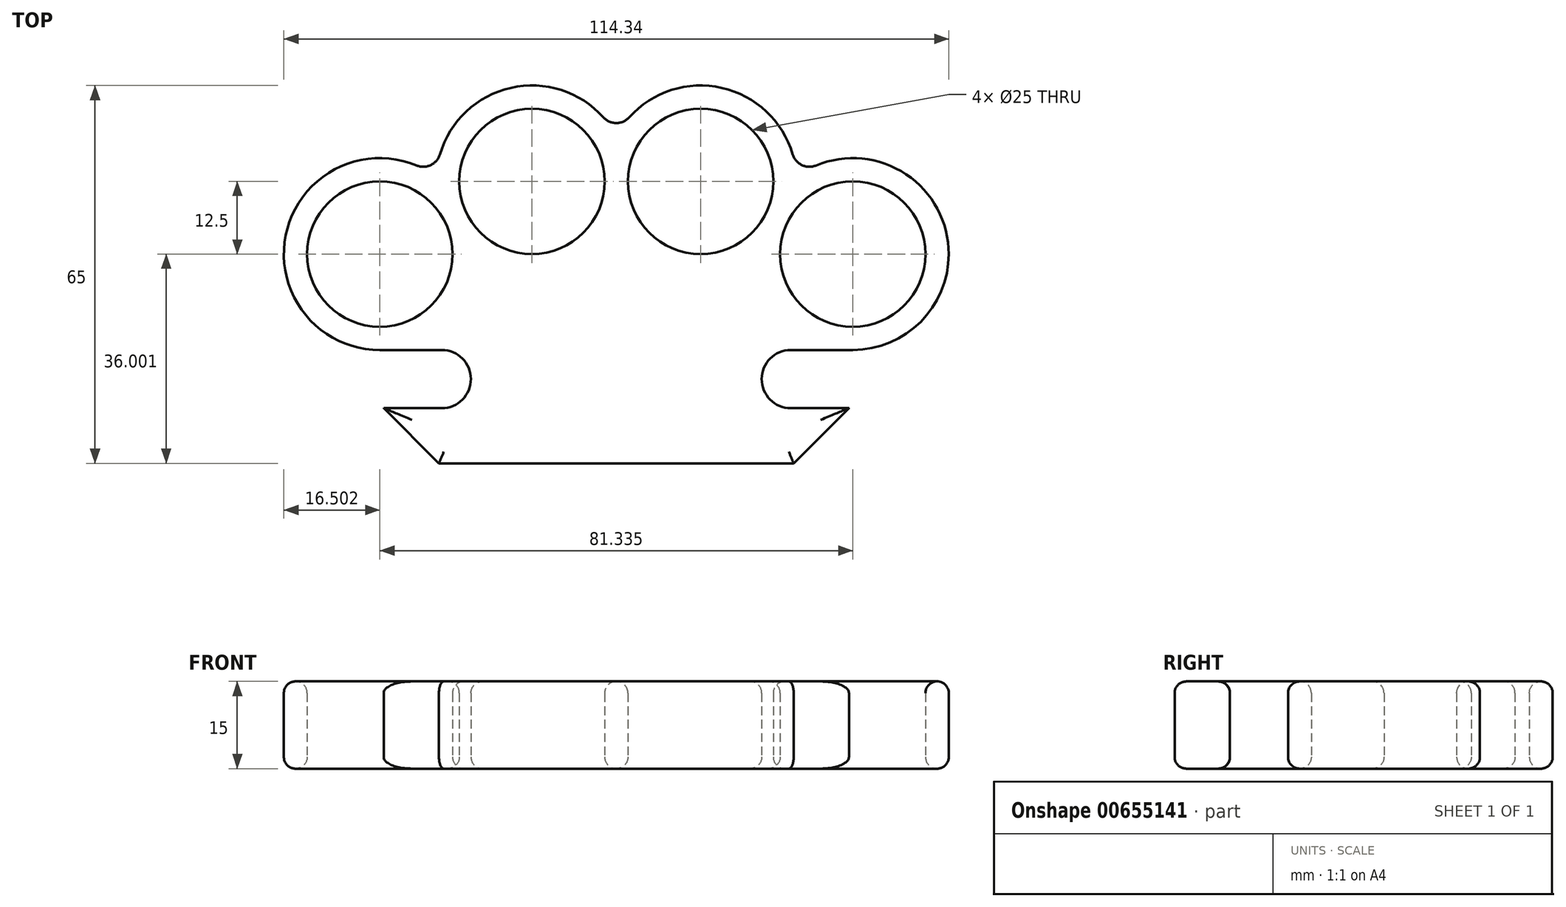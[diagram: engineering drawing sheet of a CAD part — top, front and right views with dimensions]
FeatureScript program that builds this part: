
annotation { "Feature Type Name" : "Feature", "Feature Type Description" : "" }
export const myFeature = defineFeature(function(context is Context, id is Id, definition is map)
    precondition{}
    {
        {
            var Q0;
            Q0=qCreatedBy(makeId("Top.planeOp"),FACE);
            var sketch = newSketch(context, id + "F0", { "sketchPlane" : qUnion([Q0])});
            skCircle(sketch, "E0", {"center": v(-14.5, 6.94) * mm, "radius": 12.5 * mm});
            skCircle(sketch, "E1", {"center": v(-40.67, -5.56) * mm, "radius": 12.5 * mm});
            skArc(sketch, "E2", {"start": v(-34.35, 9.68) * mm, "mid": v(-56.85, -2.34) * mm, "end": v(-40.67, -22.06) * mm});
            skArc(sketch, "E3", {"start": v(-2.23, 17.97) * mm, "mid": v(-18.15, 23.03) * mm, "end": v(-30.33, 11.6) * mm});
            skArc(sketch, "E4", {"start": v(-34.35, 9.68) * mm, "mid": v(-31.91, 9.75) * mm, "end": v(-30.33, 11.6) * mm});
            skArc(sketch, "E5", {"start": v(-30, -32.06) * mm, "mid": v(-25, -27.06) * mm, "end": v(-30, -22.06) * mm});
            skLineSegment(sketch, "E6", {"start": v(-30, -22.06) * mm, "end": v(-40.67, -22.06) * mm});
            skLineSegment(sketch, "E7", {"start": v(-30, -32.06) * mm, "end": v(-40, -32.06) * mm});
            skLineSegment(sketch, "E8", {"start": v(-40, -32.06) * mm, "end": v(-30.5, -41.56) * mm});
            skLineSegment(sketch, "E9", {"start": v(-30.5, -41.56) * mm, "end": v(0, -41.56) * mm});
            skArc(sketch, "E10", {"start": v(-2.23, 17.97) * mm, "mid": v(-1.22, 17.24) * mm, "end": v(0, 16.98) * mm});
            skArc(sketch, "E11.MirrorCS", {"start": v(2.23, 17.97) * mm, "mid": v(18.15, 23.03) * mm, "end": v(30.33, 11.6) * mm});
            skArc(sketch, "E12.MirrorCS", {"start": v(2.23, 17.97) * mm, "mid": v(1.22, 17.24) * mm, "end": v(0, 16.98) * mm});
            skCircle(sketch, "E13.MirrorC", {"center": v(14.5, 6.94) * mm, "radius": 12.5 * mm});
            skCircle(sketch, "E14.MirrorC", {"center": v(40.67, -5.56) * mm, "radius": 12.5 * mm});
            skArc(sketch, "E15.MirrorCS", {"start": v(34.35, 9.68) * mm, "mid": v(56.85, -2.34) * mm, "end": v(40.67, -22.06) * mm});
            skArc(sketch, "E16.MirrorCS", {"start": v(30, -32.06) * mm, "mid": v(25, -27.06) * mm, "end": v(30, -22.06) * mm});
            skLineSegment(sketch, "E17.MirrorCS", {"start": v(30.5, -41.56) * mm, "end": v(0, -41.56) * mm});
            skLineSegment(sketch, "E18.MirrorCS", {"start": v(30, -32.06) * mm, "end": v(40, -32.06) * mm});
            skLineSegment(sketch, "E19.MirrorCS", {"start": v(30, -22.06) * mm, "end": v(40.67, -22.06) * mm});
            skArc(sketch, "E20.MirrorCS", {"start": v(34.35, 9.68) * mm, "mid": v(31.91, 9.75) * mm, "end": v(30.33, 11.6) * mm});
            skLineSegment(sketch, "E21.MirrorCS", {"start": v(40, -32.06) * mm, "end": v(30.5, -41.56) * mm});
            skSolve(sketch);
        }
        {
            var Q0;
            Q0=makeQuery(id+"F0.imprint","IMPRINT",FACE,{"disambiguationData":[TD([[makeQuery(id+"F0.imprint","IMPRINT",EDGE,{"derivedFrom":sQuery(id+"F0.wireOp",EDGE,"E0")}),-1.0]])]});
            extrude(context, id + "F1", {"entities" : qUnion([Q0]), "depth" : 15 * mm, "offsetDistance" : 25 * mm});
        }
        {
            var Q0;
            Q0=makeQuery(id+"F1.opExtrude","CAP_EDGE",EDGE,{"disambiguationData":[OSD([sQuery(id+"F0.wireOp",EDGE,"E1")])],"isStart":false});
            var Q1;
            Q1=makeQuery(id+"F1.opExtrude","CAP_EDGE",EDGE,{"disambiguationData":[OSD([sQuery(id+"F0.wireOp",EDGE,"E1")])],"isStart":true});
            var Q2;
            Q2=makeQuery(id+"F1.opExtrude","CAP_EDGE",EDGE,{"disambiguationData":[OSD([sQuery(id+"F0.wireOp",EDGE,"E0")])],"isStart":false});
            var Q3;
            Q3=makeQuery(id+"F1.opExtrude","CAP_EDGE",EDGE,{"disambiguationData":[OSD([sQuery(id+"F0.wireOp",EDGE,"E0")])],"isStart":true});
            var Q4;
            Q4=makeQuery(id+"F1.opExtrude","CAP_EDGE",EDGE,{"disambiguationData":[OSD([sQuery(id+"F0.wireOp",EDGE,"E13.MirrorC")])],"isStart":false});
            var Q5;
            Q5=makeQuery(id+"F1.opExtrude","CAP_EDGE",EDGE,{"disambiguationData":[OSD([sQuery(id+"F0.wireOp",EDGE,"E13.MirrorC")])],"isStart":true});
            var Q6;
            Q6=makeQuery(id+"F1.opExtrude","CAP_EDGE",EDGE,{"disambiguationData":[OSD([sQuery(id+"F0.wireOp",EDGE,"E14.MirrorC")])],"isStart":false});
            var Q7;
            Q7=makeQuery(id+"F1.opExtrude","CAP_EDGE",EDGE,{"disambiguationData":[OSD([sQuery(id+"F0.wireOp",EDGE,"E14.MirrorC")])],"isStart":true});
            var Q8;
            Q8=makeQuery(id+"F1.opExtrude","CAP_EDGE",EDGE,{"disambiguationData":[OSD([sQuery(id+"F0.wireOp",EDGE,"E15.MirrorCS")])],"isStart":false});
            var Q9;
            Q9=makeQuery(id+"F1.opExtrude","CAP_EDGE",EDGE,{"disambiguationData":[OSD([sQuery(id+"F0.wireOp",EDGE,"E20.MirrorCS")])],"isStart":false});
            var Q10;
            Q10=makeQuery(id+"F1.opExtrude","CAP_EDGE",EDGE,{"disambiguationData":[OSD([sQuery(id+"F0.wireOp",EDGE,"E11.MirrorCS")])],"isStart":false});
            var Q11;
            Q11=makeQuery(id+"F1.opExtrude","CAP_EDGE",EDGE,{"disambiguationData":[OSD([sQuery(id+"F0.wireOp",EDGE,"E8")])],"isStart":false});
            var Q12;
            Q12=makeQuery(id+"F1.opExtrude","CAP_EDGE",EDGE,{"disambiguationData":[OSD([sQuery(id+"F0.wireOp",EDGE,"E9"),sQuery(id+"F0.wireOp",EDGE,"E17.MirrorCS")])],"isStart":false});
            var Q13;
            Q13=makeQuery(id+"F1.opExtrude","CAP_EDGE",EDGE,{"disambiguationData":[OSD([sQuery(id+"F0.wireOp",EDGE,"E21.MirrorCS")])],"isStart":false});
            var Q14;
            Q14=makeQuery(id+"F1.opExtrude","CAP_EDGE",EDGE,{"disambiguationData":[OSD([sQuery(id+"F0.wireOp",EDGE,"E15.MirrorCS")])],"isStart":true});
            var Q15;
            Q15=makeQuery(id+"F1.opExtrude","CAP_EDGE",EDGE,{"disambiguationData":[OSD([sQuery(id+"F0.wireOp",EDGE,"E21.MirrorCS")])],"isStart":true});
            var Q16;
            Q16=makeQuery(id+"F1.opExtrude","CAP_EDGE",EDGE,{"disambiguationData":[OSD([sQuery(id+"F0.wireOp",EDGE,"E9"),sQuery(id+"F0.wireOp",EDGE,"E17.MirrorCS")])],"isStart":true});
            var Q17;
            Q17=makeQuery(id+"F1.opExtrude","CAP_EDGE",EDGE,{"disambiguationData":[OSD([sQuery(id+"F0.wireOp",EDGE,"E8")])],"isStart":true});
            fillet(context, id + "F2", {"entities" : qUnion([Q0, Q1, Q2, Q3, Q4, Q5, Q6, Q7, Q8, Q9, Q10, Q11, Q12, Q13, Q14, Q15, Q16, Q17]), "radius" : 2 * mm, "tangentPropagation" : true, "allowEdgeOverflow" : false});
        }
    });
